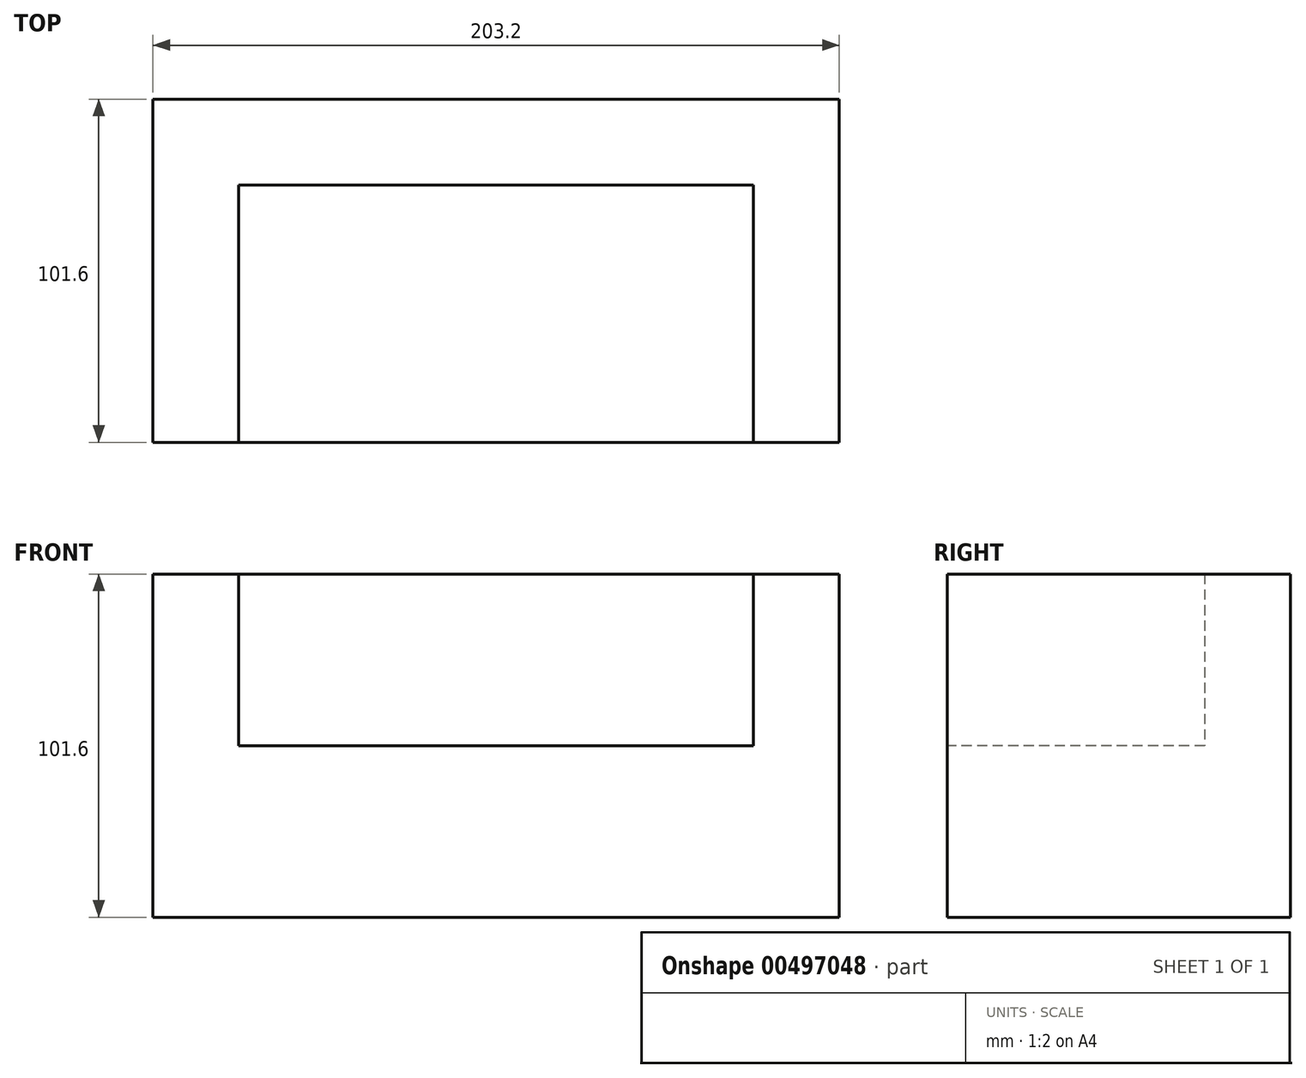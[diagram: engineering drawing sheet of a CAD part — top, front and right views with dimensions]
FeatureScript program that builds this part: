
annotation { "Feature Type Name" : "Feature", "Feature Type Description" : "" }
export const myFeature = defineFeature(function(context is Context, id is Id, definition is map)
    precondition{}
    {
        {
            var Q0;
            Q0=qCreatedBy(makeId("Front.planeOp"),FACE);
            var sketch = newSketch(context, id + "F0", { "sketchPlane" : qUnion([Q0])});
            skLineSegment(sketch, "E0", {"start": v(-66.9, -45.08) * mm, "end": v(136.3, -45.08) * mm});
            skLineSegment(sketch, "E1", {"start": v(136.3, -45.08) * mm, "end": v(136.3, 56.52) * mm});
            skLineSegment(sketch, "E2", {"start": v(136.3, 56.52) * mm, "end": v(-66.9, 56.52) * mm});
            skLineSegment(sketch, "E3", {"start": v(-66.9, 56.52) * mm, "end": v(-66.9, -45.08) * mm});
            skLineSegment(sketch, "E4", {"start": v(-66.9, 56.52) * mm, "end": v(-41.5, 56.52) * mm});
            skLineSegment(sketch, "E5", {"start": v(-41.5, 56.52) * mm, "end": v(-41.5, 5.72) * mm});
            skLineSegment(sketch, "E6", {"start": v(-41.5, 5.72) * mm, "end": v(110.9, 5.72) * mm});
            skLineSegment(sketch, "E7", {"start": v(110.9, 5.72) * mm, "end": v(110.9, 56.52) * mm});
            skSolve(sketch);
        }
        {
            var Q0;
            Q0=makeQuery(id+"F0.imprint","IMPRINT",FACE,{"disambiguationData":[TD([[makeQuery(id+"F0.imprint","IMPRINT",EDGE,{"derivedFrom":sQuery(id+"F0.wireOp",EDGE,"E0")}),1.0]])]});
            var Q1;
            {var subQ0=sQuery(id+"F0.wireOp",EDGE,"E5");Q1=makeQuery(id+"F0.imprint","IMPRINT",FACE,{"disambiguationData":[TD([[makeQuery(id+"F0.imprint","IMPRINT",EDGE,{"derivedFrom":subQ0}),1.0]])]});}
            extrude(context, id + "F1", {"entities" : qUnion([Q0, Q1]), "depth" : 101.6 * mm});
        }
        {
            var Q0;
            Q0=makeQuery(id+"F1.opExtrude","CAP_FACE",FACE,{"disambiguationData":[OSD([sQuery(id+"F0.wireOp",EDGE,"E0"),sQuery(id+"F0.wireOp",EDGE,"E1"),sQuery(id+"F0.wireOp",EDGE,"E2"),sQuery(id+"F0.wireOp",EDGE,"E3"),sQuery(id+"F0.wireOp",EDGE,"E4")])],"isStart":false});
            var sketch = newSketch(context, id + "F2", { "sketchPlane" : qUnion([Q0])});
            skLineSegment(sketch, "E8", {"start": v(-66.9, 56.52) * mm, "end": v(-41.5, 56.52) * mm});
            skLineSegment(sketch, "E9", {"start": v(-41.5, 56.52) * mm, "end": v(-41.5, 5.72) * mm});
            skLineSegment(sketch, "E10", {"start": v(-41.5, 5.72) * mm, "end": v(110.9, 5.72) * mm});
            skLineSegment(sketch, "E11", {"start": v(110.9, 5.72) * mm, "end": v(110.9, 56.52) * mm});
            skLineSegment(sketch, "E12", {"start": v(110.9, 56.52) * mm, "end": v(136.3, 56.52) * mm});
            skSolve(sketch);
        }
        {
            var Q0;
            {var subQ0=sQuery(id+"F2.wireOp",EDGE,"E9");Q0=makeQuery(id+"F2.imprint","IMPRINT",FACE,{"disambiguationData":[TD([[makeQuery(id+"F2.imprint","IMPRINT",EDGE,{"derivedFrom":subQ0}),1.0]])]});}
            extrude(context, id + "F3", {"entities" : qUnion([Q0]), "operationType" : NewBodyOperationType.REMOVE, "oppositeDirection" : true, "depth" : 76.2 * mm});
        }
    });
